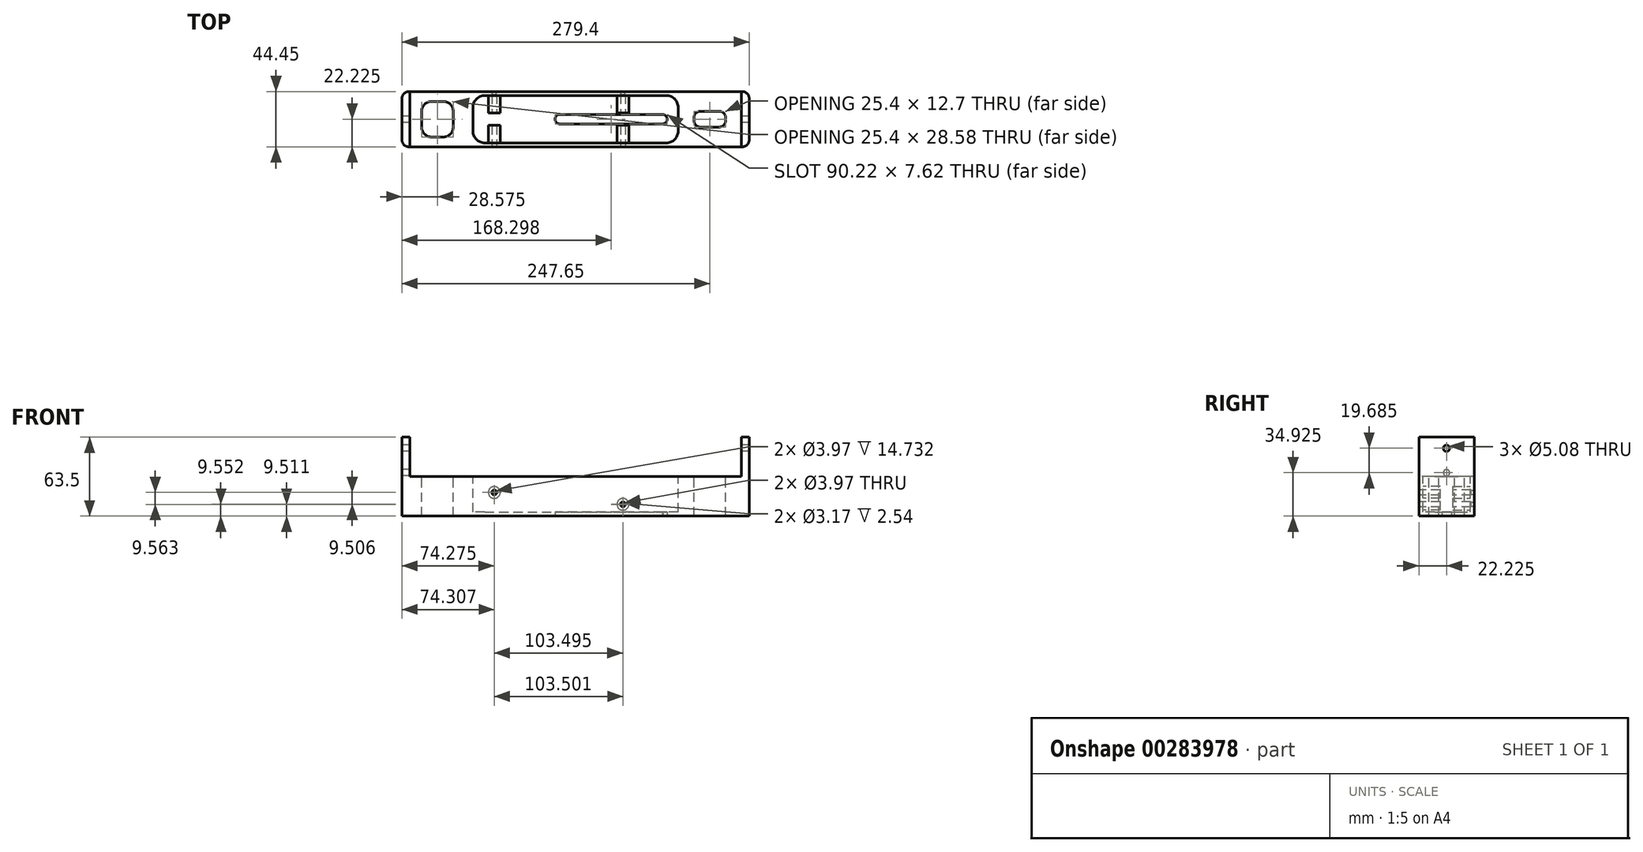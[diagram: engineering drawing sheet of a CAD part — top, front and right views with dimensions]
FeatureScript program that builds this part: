
annotation { "Feature Type Name" : "Feature", "Feature Type Description" : "" }
export const myFeature = defineFeature(function(context is Context, id is Id, definition is map)
    precondition{}
    {
        {
            var Q0;
            Q0=qCreatedBy(makeId("Top.planeOp"),FACE);
            var sketch = newSketch(context, id + "F0", { "sketchPlane" : qUnion([Q0])});
            skLineSegment(sketch, "E0.bottom", {"start": v(0, 0) * mm, "end": v(279.4, 0) * mm});
            skLineSegment(sketch, "E0.top", {"start": v(0, 44.45) * mm, "end": v(279.4, 44.45) * mm});
            skLineSegment(sketch, "E0.left", {"start": v(0, 0) * mm, "end": v(0, 44.45) * mm});
            skLineSegment(sketch, "E0.right", {"start": v(279.4, 0) * mm, "end": v(279.4, 44.45) * mm});
            skSolve(sketch);
        }
        {
            var Q0;
            Q0=makeQuery(id+"F0.imprint","IMPRINT",FACE,{"disambiguationData":[TD([[makeQuery(id+"F0.imprint","IMPRINT",EDGE,{"derivedFrom":sQuery(id+"F0.wireOp",EDGE,"E0.bottom")}),1.0]])]});
            extrude(context, id + "F1", {"entities" : qUnion([Q0]), "depth" : 31.75 * mm});
        }
        {
            var Q0;
            Q0=makeQuery(id+"F1.opExtrude","CAP_FACE",FACE,{"disambiguationData":[OSD([sQuery(id+"F0.wireOp",EDGE,"E0.bottom"),sQuery(id+"F0.wireOp",EDGE,"E0.top"),sQuery(id+"F0.wireOp",EDGE,"E0.left"),sQuery(id+"F0.wireOp",EDGE,"E0.right")])],"isStart":false});
            var sketch = newSketch(context, id + "F2", { "sketchPlane" : qUnion([Q0])});
            skLineSegment(sketch, "E1.bottom", {"start": v(57.15, 3.18) * mm, "end": v(222.25, 3.18) * mm});
            skLineSegment(sketch, "E1.top", {"start": v(57.15, 41.27) * mm, "end": v(222.25, 41.27) * mm});
            skLineSegment(sketch, "E1.left", {"start": v(57.15, 3.18) * mm, "end": v(57.15, 41.27) * mm});
            skLineSegment(sketch, "E1.right", {"start": v(222.25, 3.18) * mm, "end": v(222.25, 41.27) * mm});
            skSolve(sketch);
        }
        {
            var Q0;
            Q0 = qSketchRegion(id + "F2", true);
            extrude(context, id + "F3", {"entities" : qUnion([Q0]), "operationType" : NewBodyOperationType.REMOVE, "oppositeDirection" : true, "depth" : 28.57 * mm});
        }
        {
            var Q0;
            Q0=makeQuery(id+"F1.opExtrude","CAP_FACE",FACE,{"disambiguationData":[OSD([sQuery(id+"F0.wireOp",EDGE,"E0.bottom"),sQuery(id+"F0.wireOp",EDGE,"E0.top"),sQuery(id+"F0.wireOp",EDGE,"E0.left"),sQuery(id+"F0.wireOp",EDGE,"E0.right")])],"isStart":true});
            var sketch = newSketch(context, id + "F4", { "sketchPlane" : qUnion([Q0])});
            skArc(sketch, "E2", {"start": v(209.87, -26.03) * mm, "mid": v(213.4, -22.07) * mm, "end": v(209.55, -18.41) * mm});
            skLineSegment(sketch, "E3", {"start": v(209.55, -18.41) * mm, "end": v(127, -18.41) * mm});
            skArc(sketch, "E4", {"start": v(127, -18.41) * mm, "mid": v(123.2, -22.23) * mm, "end": v(127, -26.04) * mm});
            skLineSegment(sketch, "E5", {"start": v(127, -26.04) * mm, "end": v(209.87, -26.03) * mm});
            skSolve(sketch);
        }
        {
            var Q0;
            Q0=makeQuery(id+"F4.imprint","IMPRINT",FACE,{"disambiguationData":[TD([[makeQuery(id+"F4.imprint","IMPRINT",EDGE,{"derivedFrom":sQuery(id+"F4.wireOp",EDGE,"E2")}),1.0]])]});
            extrude(context, id + "F5", {"entities" : qUnion([Q0]), "operationType" : NewBodyOperationType.REMOVE, "endBound" : BoundingType.THROUGH_ALL, "oppositeDirection" : true, "depth" : 25.4 * mm});
        }
        {
            var Q0;
            Q0=makeQuery(id+"F2.imprint","IMPRINT",FACE,{"disambiguationData":[TD([[makeQuery(id+"F2.imprint","IMPRINT",EDGE,{"derivedFrom":sQuery(id+"F2.wireOp",EDGE,"E1.bottom")}),-1.0]])]});
            var sketch = newSketch(context, id + "F6", { "sketchPlane" : qUnion([Q0])});
            skLineSegment(sketch, "E6.bottom", {"start": v(0, 0) * mm, "end": v(6.35, 0) * mm});
            skLineSegment(sketch, "E6.top", {"start": v(0, 44.45) * mm, "end": v(6.35, 44.45) * mm});
            skLineSegment(sketch, "E6.left", {"start": v(0, 0) * mm, "end": v(0, 44.45) * mm});
            skLineSegment(sketch, "E6.right", {"start": v(6.35, 0) * mm, "end": v(6.35, 44.45) * mm});
            skLineSegment(sketch, "E7.bottom", {"start": v(279.4, 44.45) * mm, "end": v(273.05, 44.45) * mm});
            skLineSegment(sketch, "E7.top", {"start": v(279.4, 0) * mm, "end": v(273.05, 0) * mm});
            skLineSegment(sketch, "E7.left", {"start": v(279.4, 44.45) * mm, "end": v(279.4, 0) * mm});
            skLineSegment(sketch, "E7.right", {"start": v(273.05, 44.45) * mm, "end": v(273.05, 0) * mm});
            skSolve(sketch);
        }
        {
            var Q0;
            Q0 = qSketchRegion(id + "F6", true);
            extrude(context, id + "F7", {"entities" : qUnion([Q0]), "operationType" : NewBodyOperationType.ADD, "depth" : 31.75 * mm});
        }
        {
            var Q0;
            Q0=makeQuery(id+"F3.boolean.opBoolean","COPY",EDGE,{"derivedFrom":makeQuery(id+"F3.opExtrude","SWEPT_EDGE",EDGE,{"disambiguationData":[OSD([sQuery(id+"F2.wireOp",EDGE,"E1.bottom"),sQuery(id+"F2.wireOp",EDGE,"E1.left")])]})});
            var Q1;
            Q1=makeQuery(id+"F3.boolean.opBoolean","COPY",EDGE,{"derivedFrom":makeQuery(id+"F3.opExtrude","SWEPT_EDGE",EDGE,{"disambiguationData":[OSD([sQuery(id+"F2.wireOp",EDGE,"E1.top"),sQuery(id+"F2.wireOp",EDGE,"E1.left")])]})});
            var Q2;
            Q2=makeQuery(id+"F3.boolean.opBoolean","COPY",EDGE,{"derivedFrom":makeQuery(id+"F3.opExtrude","SWEPT_EDGE",EDGE,{"disambiguationData":[OSD([sQuery(id+"F2.wireOp",EDGE,"E1.bottom"),sQuery(id+"F2.wireOp",EDGE,"E1.right")])]})});
            var Q3;
            Q3=makeQuery(id+"F3.boolean.opBoolean","COPY",EDGE,{"derivedFrom":makeQuery(id+"F3.opExtrude","SWEPT_EDGE",EDGE,{"disambiguationData":[OSD([sQuery(id+"F2.wireOp",EDGE,"E1.top"),sQuery(id+"F2.wireOp",EDGE,"E1.right")])]})});
            fillet(context, id + "F8", {"entities" : qUnion([Q0, Q1, Q2, Q3]), "radius" : 9.52 * mm, "tangentPropagation" : true, "allowEdgeOverflow" : false});
        }
        {
            var Q0;
            Q0=makeQuery(id+"F7.boolean.opBoolean","MERGE",EDGE,{"derivedFrom":[makeQuery(id+"F1.opExtrude","SWEPT_EDGE",EDGE,{"disambiguationData":[OSD([sQuery(id+"F0.wireOp",EDGE,"E0.top"),sQuery(id+"F0.wireOp",EDGE,"E0.left")])]}),makeQuery(id+"F7.opExtrude","SWEPT_EDGE",EDGE,{"disambiguationData":[OSD([sQuery(id+"F6.wireOp",EDGE,"E6.top"),sQuery(id+"F6.wireOp",EDGE,"E6.left")])]})]});
            var Q1;
            Q1=makeQuery(id+"F7.boolean.opBoolean","MERGE",EDGE,{"derivedFrom":[makeQuery(id+"F1.opExtrude","SWEPT_EDGE",EDGE,{"disambiguationData":[OSD([sQuery(id+"F0.wireOp",EDGE,"E0.bottom"),sQuery(id+"F0.wireOp",EDGE,"E0.left")])]}),makeQuery(id+"F7.opExtrude","SWEPT_EDGE",EDGE,{"disambiguationData":[OSD([sQuery(id+"F6.wireOp",EDGE,"E6.bottom"),sQuery(id+"F6.wireOp",EDGE,"E6.left")])]})]});
            var Q2;
            Q2=makeQuery(id+"F7.boolean.opBoolean","MERGE",EDGE,{"derivedFrom":[makeQuery(id+"F1.opExtrude","SWEPT_EDGE",EDGE,{"disambiguationData":[OSD([sQuery(id+"F0.wireOp",EDGE,"E0.top"),sQuery(id+"F0.wireOp",EDGE,"E0.right")])]}),makeQuery(id+"F7.opExtrude","SWEPT_EDGE",EDGE,{"disambiguationData":[OSD([sQuery(id+"F6.wireOp",EDGE,"E7.bottom"),sQuery(id+"F6.wireOp",EDGE,"E7.left")])]})]});
            var Q3;
            Q3=makeQuery(id+"F7.boolean.opBoolean","MERGE",EDGE,{"derivedFrom":[makeQuery(id+"F1.opExtrude","SWEPT_EDGE",EDGE,{"disambiguationData":[OSD([sQuery(id+"F0.wireOp",EDGE,"E0.bottom"),sQuery(id+"F0.wireOp",EDGE,"E0.right")])]}),makeQuery(id+"F7.opExtrude","SWEPT_EDGE",EDGE,{"disambiguationData":[OSD([sQuery(id+"F6.wireOp",EDGE,"E7.top"),sQuery(id+"F6.wireOp",EDGE,"E7.left")])]})]});
            fillet(context, id + "F9", {"entities" : qUnion([Q0, Q1, Q2, Q3]), "radius" : 5.6 * mm, "tangentPropagation" : true, "allowEdgeOverflow" : false});
        }
        {
            var Q0;
            Q0=qCreatedBy(makeId("Right.planeOp"),FACE);
            var sketch = newSketch(context, id + "F10", { "sketchPlane" : qUnion([Q0])});
            skCircle(sketch, "E8", {"center": v(22.23, 54.6) * mm, "radius": 2.54 * mm});
            skSolve(sketch);
        }
        {
            var Q0;
            Q0=makeQuery(id+"F10.imprint","IMPRINT",FACE,{"disambiguationData":[TD([[makeQuery(id+"F10.imprint","IMPRINT",EDGE,{"derivedFrom":sQuery(id+"F10.wireOp",EDGE,"E8")}),1.0]])]});
            extrude(context, id + "F11", {"entities" : qUnion([Q0]), "operationType" : NewBodyOperationType.REMOVE, "depth" : 279.4 * mm});
        }
        {
            var Q0;
            Q0=makeQuery(id+"F2.imprint","IMPRINT",FACE,{"disambiguationData":[TD([[makeQuery(id+"F2.imprint","IMPRINT",EDGE,{"derivedFrom":sQuery(id+"F2.wireOp",EDGE,"E1.bottom")}),-1.0]])]});
            var sketch = newSketch(context, id + "F12", { "sketchPlane" : qUnion([Q0])});
            skLineSegment(sketch, "E9.bottom", {"start": v(15.88, 7.94) * mm, "end": v(41.28, 7.94) * mm});
            skLineSegment(sketch, "E9.top", {"start": v(15.88, 36.51) * mm, "end": v(41.28, 36.51) * mm});
            skLineSegment(sketch, "E9.left", {"start": v(15.88, 7.94) * mm, "end": v(15.88, 36.51) * mm});
            skLineSegment(sketch, "E9.right", {"start": v(41.28, 7.94) * mm, "end": v(41.27, 36.51) * mm});
            skLineSegment(sketch, "E10.bottom", {"start": v(234.95, 15.87) * mm, "end": v(260.35, 15.87) * mm});
            skLineSegment(sketch, "E10.top", {"start": v(234.95, 28.57) * mm, "end": v(260.35, 28.57) * mm});
            skLineSegment(sketch, "E10.left", {"start": v(234.95, 15.87) * mm, "end": v(234.95, 28.57) * mm});
            skLineSegment(sketch, "E10.right", {"start": v(260.35, 15.87) * mm, "end": v(260.35, 28.57) * mm});
            skSolve(sketch);
        }
        {
            var Q0;
            Q0 = qSketchRegion(id + "F12", true);
            extrude(context, id + "F13", {"entities" : qUnion([Q0]), "operationType" : NewBodyOperationType.REMOVE, "endBound" : BoundingType.THROUGH_ALL, "oppositeDirection" : true, "depth" : 25.4 * mm});
        }
        {
            var Q0;
            Q0=qCreatedBy(makeId("Right.planeOp"),FACE);
            var sketch = newSketch(context, id + "F14", { "sketchPlane" : qUnion([Q0])});
            skCircle(sketch, "E11", {"center": v(22.23, 34.93) * mm, "radius": 2.54 * mm});
            skSolve(sketch);
        }
        {
            var Q0;
            Q0=makeQuery(id+"F14.imprint","IMPRINT",FACE,{"disambiguationData":[TD([[makeQuery(id+"F14.imprint","IMPRINT",EDGE,{"derivedFrom":sQuery(id+"F14.wireOp",EDGE,"E11")}),1.0]])]});
            extrude(context, id + "F15", {"entities" : qUnion([Q0]), "operationType" : NewBodyOperationType.REMOVE, "depth" : 7.62 * mm});
        }
        {
            var Q0;
            Q0=makeQuery(id+"F13.boolean.opBoolean","COPY",EDGE,{"derivedFrom":makeQuery(id+"F13.opExtrude","SWEPT_EDGE",EDGE,{"disambiguationData":[OSD([sQuery(id+"F12.wireOp",EDGE,"E9.top"),sQuery(id+"F12.wireOp",EDGE,"E9.left")])]})});
            var Q1;
            Q1=makeQuery(id+"F13.boolean.opBoolean","COPY",EDGE,{"derivedFrom":makeQuery(id+"F13.opExtrude","SWEPT_EDGE",EDGE,{"disambiguationData":[OSD([sQuery(id+"F12.wireOp",EDGE,"E9.top"),sQuery(id+"F12.wireOp",EDGE,"E9.right")])]})});
            var Q2;
            Q2=makeQuery(id+"F13.boolean.opBoolean","COPY",EDGE,{"derivedFrom":makeQuery(id+"F13.opExtrude","SWEPT_EDGE",EDGE,{"disambiguationData":[OSD([sQuery(id+"F12.wireOp",EDGE,"E9.bottom"),sQuery(id+"F12.wireOp",EDGE,"E9.right")])]})});
            var Q3;
            Q3=makeQuery(id+"F13.boolean.opBoolean","COPY",EDGE,{"derivedFrom":makeQuery(id+"F13.opExtrude","SWEPT_EDGE",EDGE,{"disambiguationData":[OSD([sQuery(id+"F12.wireOp",EDGE,"E9.bottom"),sQuery(id+"F12.wireOp",EDGE,"E9.left")])]})});
            fillet(context, id + "F16", {"entities" : qUnion([Q0, Q1, Q2, Q3]), "radius" : 7.94 * mm, "tangentPropagation" : true, "allowEdgeOverflow" : false});
        }
        {
            var Q0;
            Q0=makeQuery(id+"F13.boolean.opBoolean","COPY",EDGE,{"derivedFrom":makeQuery(id+"F13.opExtrude","SWEPT_EDGE",EDGE,{"disambiguationData":[OSD([sQuery(id+"F12.wireOp",EDGE,"E10.top"),sQuery(id+"F12.wireOp",EDGE,"E10.left")])]})});
            var Q1;
            Q1=makeQuery(id+"F13.boolean.opBoolean","COPY",EDGE,{"derivedFrom":makeQuery(id+"F13.opExtrude","SWEPT_EDGE",EDGE,{"disambiguationData":[OSD([sQuery(id+"F12.wireOp",EDGE,"E10.top"),sQuery(id+"F12.wireOp",EDGE,"E10.right")])]})});
            var Q2;
            Q2=makeQuery(id+"F13.boolean.opBoolean","COPY",EDGE,{"derivedFrom":makeQuery(id+"F13.opExtrude","SWEPT_EDGE",EDGE,{"disambiguationData":[OSD([sQuery(id+"F12.wireOp",EDGE,"E10.bottom"),sQuery(id+"F12.wireOp",EDGE,"E10.right")])]})});
            var Q3;
            Q3=makeQuery(id+"F13.boolean.opBoolean","COPY",EDGE,{"derivedFrom":makeQuery(id+"F13.opExtrude","SWEPT_EDGE",EDGE,{"disambiguationData":[OSD([sQuery(id+"F12.wireOp",EDGE,"E10.bottom"),sQuery(id+"F12.wireOp",EDGE,"E10.left")])]})});
            fillet(context, id + "F17", {"entities" : qUnion([Q0, Q1, Q2, Q3]), "radius" : 5.08 * mm, "tangentPropagation" : true, "allowEdgeOverflow" : false});
        }
        {
            var Q0;
            Q0=makeQuery(id+"F7.boolean.opBoolean","MERGE",FACE,{"derivedFrom":[makeQuery(id+"F1.opExtrude","SWEPT_FACE",FACE,{"disambiguationData":[OSD([sQuery(id+"F0.wireOp",EDGE,"E0.bottom")])]}),makeQuery(id+"F7.opExtrude","SWEPT_FACE",FACE,{"disambiguationData":[OSD([sQuery(id+"F6.wireOp",EDGE,"E6.bottom")])]}),makeQuery(id+"F7.opExtrude","SWEPT_FACE",FACE,{"disambiguationData":[OSD([sQuery(id+"F6.wireOp",EDGE,"E7.top")])]})]});
            var sketch = newSketch(context, id + "F18", { "sketchPlane" : qUnion([Q0])});
            skCircle(sketch, "E12", {"center": v(177.8, 9.52) * mm, "radius": 4.76 * mm});
            skCircle(sketch, "E13", {"center": v(74.3, 19.05) * mm, "radius": 4.76 * mm});
            skSolve(sketch);
        }
        {
            var Q0;
            Q0 = qSketchRegion(id + "F18", true);
            extrude(context, id + "F19", {"entities" : qUnion([Q0]), "operationType" : NewBodyOperationType.ADD, "oppositeDirection" : true, "depth" : 17.27 * mm});
        }
        {
            var Q0;
            Q0=makeQuery(id+"F7.boolean.opBoolean","MERGE",FACE,{"derivedFrom":[makeQuery(id+"F1.opExtrude","SWEPT_FACE",FACE,{"disambiguationData":[OSD([sQuery(id+"F0.wireOp",EDGE,"E0.top")])]}),makeQuery(id+"F7.opExtrude","SWEPT_FACE",FACE,{"disambiguationData":[OSD([sQuery(id+"F6.wireOp",EDGE,"E6.top")])]}),makeQuery(id+"F7.opExtrude","SWEPT_FACE",FACE,{"disambiguationData":[OSD([sQuery(id+"F6.wireOp",EDGE,"E7.bottom")])]})]});
            var sketch = newSketch(context, id + "F20", { "sketchPlane" : qUnion([Q0])});
            skCircle(sketch, "E14", {"center": v(-177.8, 9.52) * mm, "radius": 4.76 * mm});
            skCircle(sketch, "E15", {"center": v(-74.3, 19.05) * mm, "radius": 4.76 * mm});
            skSolve(sketch);
        }
        {
            var Q0;
            Q0 = qSketchRegion(id + "F20", true);
            extrude(context, id + "F21", {"entities" : qUnion([Q0]), "operationType" : NewBodyOperationType.ADD, "oppositeDirection" : true, "depth" : 17.27 * mm});
        }
        {
            var Q0;
            Q0=makeQuery(id+"F18.imprint","IMPRINT",FACE,{"disambiguationData":[TD([[makeQuery(id+"F18.imprint","IMPRINT",EDGE,{"derivedFrom":sQuery(id+"F18.wireOp",EDGE,"E12")}),-1.0]])]});
            var sketch = newSketch(context, id + "F22", { "sketchPlane" : qUnion([Q0])});
            skCircle(sketch, "E16", {"center": v(74.3, 19.07) * mm, "radius": 1.98 * mm});
            skCircle(sketch, "E17", {"center": v(177.8, 9.51) * mm, "radius": 1.98 * mm});
            skSolve(sketch);
        }
        {
            var Q0;
            Q0 = qSketchRegion(id + "F22", true);
            extrude(context, id + "F23", {"entities" : qUnion([Q0]), "operationType" : NewBodyOperationType.REMOVE, "oppositeDirection" : true, "depth" : 41.9 * mm});
        }
        {
            var Q0;
            Q0=makeQuery(id+"F20.imprint","IMPRINT",FACE,{"disambiguationData":[TD([[makeQuery(id+"F20.imprint","IMPRINT",EDGE,{"derivedFrom":sQuery(id+"F20.wireOp",EDGE,"E14")}),-1.0]])]});
            var sketch = newSketch(context, id + "F24", { "sketchPlane" : qUnion([Q0])});
            skCircle(sketch, "E18", {"center": v(-177.77, 9.55) * mm, "radius": 1.59 * mm});
            skCircle(sketch, "E19", {"center": v(-74.27, 19.06) * mm, "radius": 1.59 * mm});
            skSolve(sketch);
        }
        {
            var Q0;
            Q0 = qSketchRegion(id + "F24", true);
            extrude(context, id + "F25", {"entities" : qUnion([Q0]), "operationType" : NewBodyOperationType.REMOVE, "oppositeDirection" : true, "depth" : 3.17 * mm});
        }
    });
